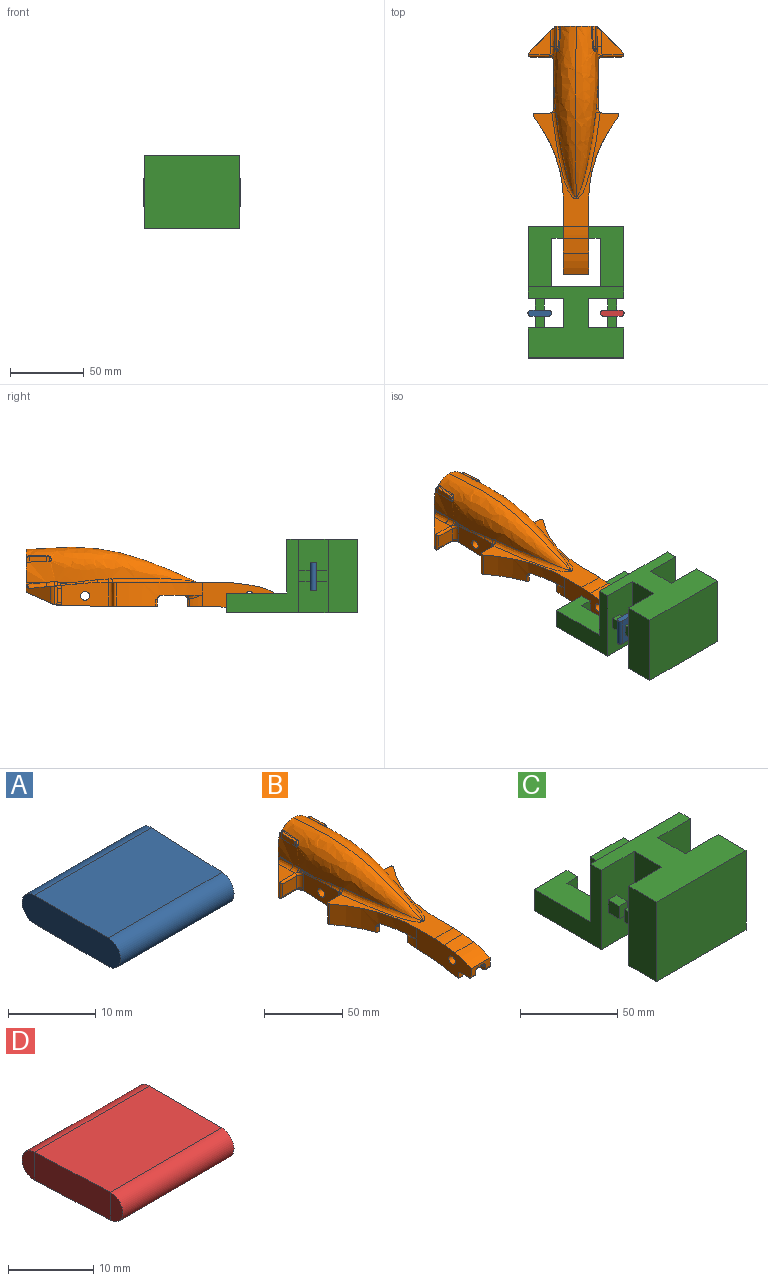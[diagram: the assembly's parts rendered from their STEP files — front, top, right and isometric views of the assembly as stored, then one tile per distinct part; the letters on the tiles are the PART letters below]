
ASSEMBLY  parts=4 mates=3
PART A: 8 faces, bbox 19.1x16x4 mm
  f0: cylinder r=2mm len=18.48mm, axis (-1,0,0), area 115.8mm2, adj f1,f3,f4,f5
  f1: plane 18.99x12mm, normal (0,0,1), area 224.7mm2, adj f0,f2,f4,f6
  f2: cylinder r=2mm len=19.09mm, axis (-1,0,0), area 119.7mm2, adj f1,f3,f4,f7
  f3: plane 18.99x12mm, normal (0,0,-1), area 224.7mm2, adj f0,f2,f4,f6
  f4: plane 16x4mm, normal (-1,0,0), area 60.6mm2, adj f0,f1,f2,f3
  f5: plane 4x2mm, normal (1,-0.04,0), area 6.3mm2, adj f0,f6
  f6: extruded ~12x4mm, area 48mm2, adj f1,f3,f5,f7
  f7: plane 4x2mm, normal (1,-0.05,0), area 6.3mm2, adj f2,f6
PART B: 206 faces, bbox 65.7x176.7x49.3 mm
  f0: extruded ~13.86x1.47mm, area 8mm2, adj f153,f156,f180,f181
  f1: extruded ~13.86x1.47mm, area 8mm2, adj f153,f154,f200,f201
  f2: plane 4.04x2.22mm, normal (-1,0.05,0), area 7.2mm2, adj f154,f158,f159,f167,f179
  f3: plane 3.74x2.02mm, normal (-1,0.04,0), area 6.6mm2, adj f4,f154,f158,f166,f174
  f4: plane 1.69x0.12mm, normal (0,-1,0), area 0.1mm2, adj f3,f154,f174
  f5: plane 12x2.55mm, normal (0,0,1), area 21.9mm2, adj f158,f166,f167,f176
  f6: plane 3.74x2.02mm, normal (1,0.04,0), area 6.6mm2, adj f156,f160,f161,f165,f168
  f7: plane 4.04x2.22mm, normal (1,0.05,0), area 7.2mm2, adj f8,f156,f160,f164,f173
  f8: plane 0.69x0.38mm, normal (0,1,0), area 0.1mm2, adj f7,f164,f173
  f9: plane 12x2.55mm, normal (0,0,1), area 21.9mm2, adj f160,f164,f165,f170
  f10: cylinder r=1.5mm len=7.39mm, axis (-1,0,0), area 10mm2, adj f93,f94,f141,f153
  f11: plane 77.19x58.27mm, normal (0,0,1), area 850.3mm2, adj f37,f38,f43,f45,f46,f47,f51,f52
  f12: cylinder r=1.5mm len=7.39mm, axis (-1,0,0), area 10mm2, adj f27,f84,f129,f153
  f13: plane 16.53x15.09mm, normal (0,0.09,1), area 127mm2, adj f94,f95,f96,f97,f144,f181,f182
  f14: cylinder r=3mm len=17mm, axis (-1,0,0), area 320.4mm2, adj f37,f38
  f15: plane 12.39x5.01mm, normal (0,-0.38,-0.93), area 40.5mm2, adj f16,f69,f99,f100,f101,f109,f110,f111
  f16: cylinder r=3mm len=9.64mm, axis (0,0.93,-0.38), area 38.5mm2, adj f15,f35,f39,f99,f150,f151
  f17: plane 32.43x16.02mm, normal (-1,0,0), area 455.3mm2, adj f31,f44,f64,f76,f82,f145,f146,f147
  f18: plane 17.44x4.22mm, normal (-1,0,0), area 15.6mm2, adj f92,f93,f98,f141
  f19: plane 17.44x4.22mm, normal (1,0,0), area 15.6mm2, adj f27,f28,f82,f129
  f20: plane 8.07x3.26mm, normal (-1,0,0), area 12.7mm2, adj f35,f61,f66,f109
  f21: plane 46.27x9mm, normal (1,0,0), area 142.9mm2, adj f41,f59,f67,f77,f78,f101,f102,f103
  f22: plane 38.6x16.7mm, normal (0,0.24,-0.97), area 601mm2, adj f71,f129,f130,f140,f141,f153
  f23: plane 28.21x4.5mm, normal (1,0,0), area 94.2mm2, adj f31,f50,f76,f123,f124,f125
  f24: cylinder r=30mm len=4.5mm, axis (0,0,-1), area 0.2mm2, adj f32,f54,f75,f133
  f25: plane 12.69x9.72mm, normal (0,-1,0), area 123.3mm2, adj f28,f30,f83,f146
  f26: plane 16.53x15.09mm, normal (0,0.09,1), area 127mm2, adj f30,f84,f85,f87,f147,f199,f200
  f27: plane 22.85x18.63mm, normal (0,0.41,-0.91), area 265.4mm2, adj f12,f19,f28,f84,f85,f129
  f28: cylinder r=1.5mm len=21.69mm, axis (-1,0,0), area 45.4mm2, adj f19,f25,f27,f29,f82,f83,f85,f86
  f29: plane 12.72x0.14mm, normal (-1,0,0), area 1.8mm2, adj f28,f30,f83,f86
  f30: cylinder r=1.5mm len=14.19mm, axis (1,0,0), area 34.1mm2, adj f25,f26,f29,f83,f86,f147
  f31: cylinder r=41.69mm len=4.5mm, axis (1,0,0), area 6.5mm2, adj f17,f23,f76,f82,f126
  f32: plane 28.21x4.5mm, normal (-1,0,0), area 94.2mm2, adj f24,f75,f81,f134,f135,f136
  f33: plane 51.59x25.23mm, normal (0,0,-1), area 736.5mm2, adj f45,f51,f73,f74,f105,f106,f116,f117
  f34: plane 46.27x9mm, normal (-1,0,0), area 142.9mm2, adj f40,f56,f65,f79,f80,f112,f113,f114
  f35: plane 17.01x6.48mm, normal (0,-1,0), area 69.2mm2, adj f16,f20,f37,f38,f39,f60,f61,f62
  f36: plane 32.44x16.02mm, normal (1,0,0), area 455.3mm2, adj f44,f63,f75,f81,f98,f142,f143,f144
  f37: plane 49.36x20.5mm, normal (-1,0,0), area 732.8mm2, adj f11,f14,f35,f41,f42,f43,f45,f58
  f38: plane 49.36x20.5mm, normal (1,0,0), area 732.8mm2, adj f11,f14,f35,f40,f42,f43,f51,f57
  f39: plane 8.07x3.26mm, normal (1,0,0), area 12.7mm2, adj f16,f35,f62,f68
  f40: plane 4x4mm, normal (0,-1,0), area 16mm2, adj f34,f38,f65,f79
  f41: plane 4x4mm, normal (0,-1,0), area 16mm2, adj f21,f37,f67,f78
  f42: plane 17x9.65mm, normal (0,-0.14,0.99), area 165.7mm2, adj f37,f38,f43,f60
  f43: cylinder r=60mm len=17mm, axis (1,0,0), area 144.7mm2, adj f11,f37,f38,f42
  f44: cylinder r=3mm len=30mm, axis (-1,0,0), area 565.5mm2, adj f17,f36
  f45: cylinder r=92.82mm len=57.94mm, axis (0,0,1), area 767.9mm2, adj f11,f33,f37,f47,f49,f76,f107,f108
  f46: plane 16x9.64mm, normal (0,1,0), area 154.2mm2, adj f11,f47,f64,f76
  f47: cylinder r=1.5mm len=16mm, axis (0,0,1), area 53.9mm2, adj f11,f45,f46,f76
  f48: cylinder r=136.18mm len=12.06mm, axis (0,0,-1), area 54.3mm2, adj f49,f50,f76,f121
  f49: cylinder r=1.5mm len=4.5mm, axis (0,0,1), area 18.3mm2, adj f45,f48,f76,f120
  f50: cylinder r=30mm len=4.5mm, axis (0,0,-1), area 0.2mm2, adj f23,f48,f76,f122
  f51: cylinder r=92.82mm len=57.94mm, axis (0,0,1), area 767.9mm2, adj f11,f33,f38,f53,f55,f75,f118,f119
  f52: plane 16x9.64mm, normal (0,1,0), area 154.2mm2, adj f11,f53,f63,f75
  f53: cylinder r=1.5mm len=16mm, axis (0,0,1), area 53.9mm2, adj f11,f51,f52,f75
  f54: cylinder r=136.18mm len=12.06mm, axis (0,0,-1), area 54.3mm2, adj f24,f55,f75,f132
  f55: cylinder r=1.5mm len=4.5mm, axis (0,0,1), area 18.3mm2, adj f51,f54,f75,f131
  f56: cylinder r=1.5mm len=4.84mm, axis (0,0,-1), area 19.8mm2, adj f34,f57,f80,f117,f118
  f57: cylinder r=37.75mm len=8.81mm, axis (0,0,-1), area 54.8mm2, adj f38,f56,f80,f119
  f58: cylinder r=37.75mm len=8.81mm, axis (0,0,-1), area 54.8mm2, adj f37,f59,f77,f108
  f59: cylinder r=1.5mm len=4.84mm, axis (0,0,-1), area 19.8mm2, adj f21,f58,f77,f106,f107
  f60: cylinder r=42.58mm len=17mm, axis (-1,0,0), area 268.4mm2, adj f35,f37,f38,f42
  f61: cylinder r=1.5mm len=4mm, axis (-1,0,0), area 9.4mm2, adj f20,f35,f38,f66
  f62: cylinder r=1.5mm len=4mm, axis (-1,0,0), area 9.4mm2, adj f35,f37,f39,f68
  f63: cylinder r=3mm len=16mm, axis (0,0,1), area 75.4mm2, adj f11,f36,f52,f75,f189
  f64: cylinder r=3mm len=16mm, axis (0,0,1), area 75.4mm2, adj f11,f17,f46,f76,f192
  f65: cylinder r=1.5mm len=4mm, axis (-1,0,0), area 9.4mm2, adj f34,f38,f40,f66,f111
  f66: plane 8.57x4.03mm, normal (0,0,-1), area 34.2mm2, adj f20,f38,f61,f65,f110
  f67: cylinder r=1.5mm len=4mm, axis (-1,0,0), area 9.4mm2, adj f21,f37,f41,f68,f100
  f68: plane 8.57x4.03mm, normal (0,0,-1), area 34.2mm2, adj f37,f39,f62,f67,f99
  f69: cylinder r=6mm len=3.81mm, axis (1,0,0), area 11.6mm2, adj f15,f70,f102,f113
  f70: plane 17.07x4.58mm, normal (0,0.26,-0.97), area 53mm2, adj f69,f74,f103,f114
  f71: cylinder r=6mm len=16.69mm, axis (1,0,0), area 55.6mm2, adj f22,f72,f128,f139
  f72: plane 16.03x10.19mm, normal (0,-0.32,-0.95), area 163.1mm2, adj f71,f73,f125,f126,f127,f136,f137,f138
  f73: cylinder r=50mm len=16.18mm, axis (-1,0,0), area 247.2mm2, adj f33,f72,f124,f135
  f74: cylinder r=50mm len=12.97mm, axis (1,0,0), area 39.3mm2, adj f33,f70,f104,f115
  f75: plane 40.66x18.64mm, normal (0,0,-1), area 358mm2, adj f24,f32,f36,f51,f52,f53,f54,f55
  f76: plane 40.66x18.64mm, normal (0,0,-1), area 358mm2, adj f17,f23,f31,f45,f46,f47,f48,f49
  f77: plane 9.96x4mm, normal (0,0,-1), area 34.7mm2, adj f21,f58,f59,f78
  f78: cylinder r=161.13mm len=37.81mm, axis (-1,0,0), area 152.7mm2, adj f21,f37,f41,f77
  f79: cylinder r=161.13mm len=37.81mm, axis (-1,0,0), area 152.7mm2, adj f34,f38,f40,f80
  f80: plane 9.96x4mm, normal (0,0,-1), area 34.7mm2, adj f34,f56,f57,f79
  f81: cylinder r=41.69mm len=4.5mm, axis (1,0,0), area 6.5mm2, adj f32,f36,f75,f98,f137
  f82: plane 28.76x8.77mm, normal (0,0.03,-1), area 127.9mm2, adj f17,f19,f28,f31,f127,f128,f130,f145
  f83: cylinder r=1.5mm len=12.72mm, axis (0,0,1), area 26.4mm2, adj f25,f28,f29,f30
  f84: plane 17.79x17.79mm, normal (-0.71,0.71,0), area 163.3mm2, adj f12,f26,f27,f85,f153,f200,f201
  f85: cylinder r=6mm len=12.61mm, axis (0,0,1), area 33.8mm2, adj f26,f27,f28,f84,f87
  f86: plane 12.7x0.01mm, normal (0,1,0), area 0.1mm2, adj f28,f29,f30,f87
  f87: cylinder r=1.5mm len=12.7mm, axis (0,0,1), area 4.2mm2, adj f26,f28,f85,f86
  f88: plane 12.7x0.01mm, normal (0,1,0), area 0.1mm2, adj f89,f92,f96,f97
  f89: plane 12.72x0.14mm, normal (1,0,0), area 1.8mm2, adj f88,f90,f92,f97
  f90: cylinder r=1.5mm len=12.72mm, axis (0,0,1), area 26.4mm2, adj f89,f91,f92,f97
  f91: plane 12.69x9.72mm, normal (0,-1,0), area 123.3mm2, adj f90,f92,f97,f143
  f92: cylinder r=1.5mm len=21.69mm, axis (1,0,0), area 45.4mm2, adj f18,f88,f89,f90,f91,f93,f95,f96
  f93: plane 22.85x18.63mm, normal (0,0.41,-0.91), area 265.4mm2, adj f10,f18,f92,f94,f95,f141
  f94: plane 17.78x17.78mm, normal (0.71,0.71,0), area 163.3mm2, adj f10,f13,f93,f95,f153,f180,f181
  f95: cylinder r=6mm len=12.61mm, axis (0,0,1), area 33.8mm2, adj f13,f92,f93,f94,f96
  f96: cylinder r=1.5mm len=12.7mm, axis (0,0,1), area 4.2mm2, adj f13,f88,f92,f95
  f97: cylinder r=1.5mm len=14.19mm, axis (-1,0,0), area 34.1mm2, adj f13,f88,f89,f90,f91,f144
  f98: plane 28.76x8.77mm, normal (0,0.03,-1), area 127.9mm2, adj f18,f36,f81,f92,f138,f139,f140,f142
  f99: bspline ~3.57x3.08mm, area 8.4mm2, adj f15,f16,f68,f100
  f100: bspline ~3.59x3.03mm, area 7.3mm2, adj f15,f67,f99,f101
  f101: cylinder r=3mm len=3.72mm, axis (0,0.93,-0.38), area 11.8mm2, adj f15,f21,f100,f102
  f102: torus R=9mm, axis (-1,0,0), area 21.6mm2, adj f21,f69,f101,f103
  f103: cylinder r=3mm len=17.85mm, axis (0,0.97,0.26), area 83.3mm2, adj f21,f70,f102,f104
  f104: torus R=47mm, axis (-1,0,0), area 60.5mm2, adj f21,f74,f103,f105
  f105: cylinder r=3mm len=8.98mm, axis (0,-1,0), area 42.3mm2, adj f21,f33,f104,f106
  f106: torus R=4.5mm, axis (0,0,1), area 28.9mm2, adj f33,f59,f105,f107
  f107: bspline ~3x2.79mm, area 3.8mm2, adj f45,f59,f106,f108
  f108: bspline ~10.19x2.76mm, area 10.1mm2, adj f45,f58,f107
  f109: cylinder r=3mm len=9.64mm, axis (0,0.93,-0.38), area 38.5mm2, adj f15,f20,f35,f110,f148,f149
  f110: bspline ~5.08x3.46mm, area 8.4mm2, adj f15,f66,f109,f111
  f111: bspline ~3.59x3.03mm, area 7.3mm2, adj f15,f65,f110,f112
  f112: cylinder r=3mm len=3.72mm, axis (0,0.93,-0.38), area 11.8mm2, adj f15,f34,f111,f113
  f113: torus R=9mm, axis (1,0,0), area 21.6mm2, adj f34,f69,f112,f114
  f114: cylinder r=3mm len=17.85mm, axis (0,0.97,0.26), area 83.3mm2, adj f34,f70,f113,f115
  f115: torus R=47mm, axis (1,0,0), area 60.5mm2, adj f34,f74,f114,f116
  f116: cylinder r=3mm len=8.98mm, axis (0,1,0), area 42.3mm2, adj f33,f34,f115,f117
  f117: torus R=4.5mm, axis (0,0,1), area 28.9mm2, adj f33,f56,f116,f118
  f118: bspline ~3x2.79mm, area 3.8mm2, adj f51,f56,f117,f119
  f119: bspline ~10.19x2.76mm, area 10.1mm2, adj f51,f57,f118
  f120: torus R=4.5mm, axis (0,0,1), area 24.2mm2, adj f33,f45,f49,f121
  f121: torus R=139.18mm, axis (0,0,1), area 57.4mm2, adj f33,f48,f120,f122
  f122: torus R=33mm, axis (0,0,1), area 0.2mm2, adj f33,f50,f121,f123
  f123: cylinder r=3mm len=7.28mm, axis (0,-1,0), area 34.3mm2, adj f23,f33,f122,f124
  f124: torus R=47mm, axis (-1,0,0), area 76mm2, adj f23,f73,f123,f125
  f125: cylinder r=3mm len=6.7mm, axis (0,0.95,-0.32), area 28.5mm2, adj f23,f72,f124,f126
  f126: bspline ~3x2.84mm, area 1.9mm2, adj f31,f72,f125,f127
  f127: bspline ~6.39x3.02mm, area 15.1mm2, adj f72,f82,f126,f128
  f128: bspline ~5.87x2.57mm, area 9.8mm2, adj f71,f82,f127,f130
  f129: cylinder r=3mm len=29.22mm, axis (0,-0.97,-0.24), area 121.9mm2, adj f12,f19,f22,f27,f130,f204
  f130: bspline ~10.78x3.27mm, area 36.9mm2, adj f22,f82,f128,f129
  f131: torus R=4.5mm, axis (0,0,1), area 24.2mm2, adj f33,f51,f55,f132
  f132: torus R=139.18mm, axis (0,0,1), area 57.4mm2, adj f33,f54,f131,f133
  f133: torus R=33mm, axis (0,0,1), area 0.2mm2, adj f24,f33,f132,f134
  f134: cylinder r=3mm len=7.28mm, axis (0,1,0), area 34.3mm2, adj f32,f33,f133,f135
  f135: torus R=47mm, axis (1,0,0), area 76mm2, adj f32,f73,f134,f136
  f136: cylinder r=3mm len=6.7mm, axis (0,0.95,-0.32), area 28.5mm2, adj f32,f72,f135,f137
  f137: bspline ~3.19x3.04mm, area 2mm2, adj f72,f81,f136,f138
  f138: bspline ~6.42x3.08mm, area 15.1mm2, adj f72,f98,f137,f139
  f139: bspline ~5.01x2.49mm, area 9.8mm2, adj f71,f98,f138,f140
  f140: bspline ~12.73x3.61mm, area 36.9mm2, adj f22,f98,f139,f141
  f141: cylinder r=3mm len=29.22mm, axis (0,-0.97,-0.24), area 121.9mm2, adj f10,f18,f22,f93,f140,f203
  f142: torus R=4.5mm, axis (-1,0,0), area 10.6mm2, adj f36,f92,f98,f143
  f143: cylinder r=3mm len=9.72mm, axis (0,0,1), area 45.8mm2, adj f36,f91,f142,f144
  f144: torus R=4.5mm, axis (-1,0,0), area 9.3mm2, adj f13,f36,f97,f143,f183,f184
  f145: torus R=4.5mm, axis (1,0,0), area 10.6mm2, adj f17,f28,f82,f146
  f146: cylinder r=3mm len=9.72mm, axis (0,0,1), area 45.8mm2, adj f17,f25,f145,f147
  f147: torus R=4.5mm, axis (1,0,0), area 9.3mm2, adj f17,f26,f30,f146,f197,f198
  f148: extruded ~4.21x2.6mm, area 9mm2, adj f15,f109,f149,f150,f152
  f149: extruded ~0.17x0.06mm, area 0mm2, adj f109,f148,f152
  f150: extruded ~4.21x2.6mm, area 9.1mm2, adj f15,f16,f148,f151,f152
  f151: extruded ~0.17x0.06mm, area 0mm2, adj f16,f150,f152
  f152: plane 8.57x1.99mm, normal (0,-1,0), area 7.2mm2, adj f35,f148,f149,f150,f151
  f153: plane 28.14x28.14mm, normal (0,1,0), area 416.3mm2, adj f0,f1,f10,f12,f22,f84,f94,f154
  f154: bspline ~127x31.96mm, area 2576.2mm2, adj f1,f2,f3,f4,f153,f155,f156,f158
  f155: extruded ~11.89x0.9mm, area 5.3mm2, adj f154,f196,f197
  f156: bspline ~127x31.96mm, area 2576.2mm2, adj f0,f6,f7,f153,f154,f157,f160,f161
  f157: extruded ~11.89x0.9mm, area 5.3mm2, adj f156,f184,f185
  f158: extruded ~12x3.96mm, area 46.2mm2, adj f2,f3,f5,f154
  f159: plane 0.69x0.38mm, normal (0,1,0), area 0.1mm2, adj f2,f167,f179
  f160: extruded ~12x3.96mm, area 46.2mm2, adj f6,f7,f9,f156
  f161: plane 1.69x0.12mm, normal (0,-1,0), area 0.1mm2, adj f6,f156,f168
  f162: cylinder r=9.5mm len=52mm, axis (0,1,0), area 3103.9mm2, adj f153,f163
  f163: plane 19x19mm, normal (0,1,0), area 283.5mm2, adj f162
  f164: cylinder r=2mm len=2.05mm, axis (1,0,0), area 4.3mm2, adj f7,f8,f9,f171,f172
  f165: cylinder r=2mm len=1.94mm, axis (1,0,0), area 2.2mm2, adj f6,f9,f169
  f166: cylinder r=2mm len=1.94mm, axis (-1,0,0), area 2.2mm2, adj f3,f5,f175
  f167: cylinder r=2mm len=2.05mm, axis (-1,0,0), area 4.3mm2, adj f2,f5,f159,f177,f178
  f168: bspline ~2.16x1.32mm, area 1.8mm2, adj f6,f156,f161,f169
  f169: bspline ~3.49x2.7mm, area 4.1mm2, adj f156,f165,f168,f170
  f170: bspline ~18.69x2.11mm, area 10.2mm2, adj f9,f156,f169,f171
  f171: bspline ~3.11x1.85mm, area 2mm2, adj f156,f164,f170,f172
  f172: bspline ~2.59x2.33mm, area 1.3mm2, adj f153,f164,f171,f173
  f173: bspline ~4.3x2.69mm, area 0.8mm2, adj f7,f8,f153,f172
  f174: bspline ~2.16x1.32mm, area 1.8mm2, adj f3,f4,f154,f175
  f175: bspline ~3.49x2.7mm, area 4.1mm2, adj f154,f166,f174,f176
  f176: bspline ~16.2x1.9mm, area 10.2mm2, adj f5,f154,f175,f177
  f177: bspline ~3.11x1.85mm, area 2mm2, adj f154,f167,f176,f178
  f178: bspline ~2.59x2.33mm, area 1.3mm2, adj f153,f167,f177,f179
  f179: bspline ~3.82x2.17mm, area 0.8mm2, adj f2,f153,f159,f178
  f180: bspline ~3.25x3.09mm, area 1.4mm2, adj f0,f94,f181
  f181: bspline ~31.24x5.91mm, area 58.4mm2, adj f0,f13,f94,f180,f182
  f182: bspline ~19.48x4.8mm, area 26.3mm2, adj f13,f156,f181,f183
  f183: bspline ~3.01x3mm, area 6.5mm2, adj f144,f156,f182,f184
  f184: bspline ~2.9x2.43mm, area 4.8mm2, adj f144,f157,f183,f185
  f185: bspline ~10.39x2.18mm, area 12.8mm2, adj f36,f157,f184,f186
  f186: bspline ~5.5x1.91mm, area 7.2mm2, adj f36,f156,f185,f187
  f187: bspline ~26.16x4.72mm, area 17mm2, adj f36,f156,f186,f188
  f188: bspline ~11.15x2.64mm, area 18.7mm2, adj f36,f156,f187,f189
  f189: bspline ~3.11x3.11mm, area 8.8mm2, adj f63,f156,f188,f190
  f190: bspline ~68.92x18.36mm, area 252.7mm2, adj f11,f156,f189,f191
  f191: bspline ~68.92x17.55mm, area 252.7mm2, adj f11,f154,f190,f192
  f192: bspline ~3.11x3.11mm, area 8.8mm2, adj f64,f154,f191,f193
  f193: bspline ~11.15x2.64mm, area 18.7mm2, adj f17,f154,f192,f194
  f194: bspline ~19.22x3.73mm, area 17mm2, adj f17,f154,f193,f195
  f195: bspline ~5.5x1.91mm, area 7.2mm2, adj f17,f154,f194,f196
  f196: bspline ~10.39x2.18mm, area 12.8mm2, adj f17,f155,f195,f197
  f197: bspline ~3.46x2.58mm, area 4.8mm2, adj f147,f155,f196,f198
  f198: bspline ~3.01x3mm, area 6.5mm2, adj f147,f154,f197,f199
  f199: bspline ~5.77x3.51mm, area 26.3mm2, adj f26,f154,f198,f200
  f200: bspline ~31.24x5.91mm, area 58.4mm2, adj f1,f26,f84,f199,f201
  f201: bspline ~3.25x3.09mm, area 1.4mm2, adj f1,f84,f200
  f202: plane 1.5x1.5mm, normal (-1,0,0), area 1.8mm2, adj f203
  f203: cylinder r=0.75mm len=5.34mm, axis (1,0,0), area 23mm2, adj f141,f202
  f204: cylinder r=0.75mm len=5.34mm, axis (1,0,0), area 23mm2, adj f129,f205
  f205: plane 1.5x1.5mm, normal (1,0,0), area 1.8mm2, adj f204
PART C: 46 faces, bbox 65x89.3x50 mm
  f0: plane 50x20.26mm, normal (1,0,0), area 1013.2mm2, adj f2,f7,f8,f25
  f1: plane 50x20.26mm, normal (-1,0,0), area 1013.2mm2, adj f2,f7,f8,f20
  f2: plane 65x48.26mm, normal (0,0,1), area 2177.2mm2, adj f0,f1,f3,f5,f6,f8,f20,f21
  f3: plane 65x50mm, normal (0,1,0), area 2818.9mm2, adj f2,f4,f5,f6,f7,f10,f14,f16
  f4: plane 41x13.47mm, normal (-1,0,0), area 488.4mm2, adj f3,f7,f9,f10,f12,f13
  f5: plane 50x49mm, normal (1,0,0), area 952.4mm2, adj f2,f3,f7,f9,f10,f23
  f6: plane 50x49mm, normal (-1,0,0), area 952.4mm2, adj f2,f3,f7,f15,f16,f22
  f7: plane 89.26x65mm, normal (0,0,-1), area 3489.2mm2, adj f0,f1,f3,f4,f5,f6,f8,f9
  f8: plane 65x50mm, normal (0,-1,0), area 3250mm2, adj f0,f1,f2,f7
  f9: plane 24x13.47mm, normal (0,1,0), area 279.6mm2, adj f4,f5,f7,f10,f11,f12
  f10: plane 41x24mm, normal (0,0,1), area 720mm2, adj f3,f4,f5,f9,f11,f13
  f11: plane 8x8mm, normal (-1,0,0), area 64mm2, adj f9,f10,f12,f13
  f12: plane 8x8mm, normal (0,0,-1), area 64mm2, adj f4,f9,f11,f13
  f13: plane 8x8mm, normal (0,-1,0), area 64mm2, adj f4,f10,f11,f12
  f14: plane 41x13.47mm, normal (1,0,0), area 488.4mm2, adj f3,f7,f15,f16,f18,f19
  f15: plane 24x13.47mm, normal (0,1,0), area 279.6mm2, adj f6,f7,f14,f16,f17,f18
  f16: plane 41x24mm, normal (0,0,1), area 720mm2, adj f3,f6,f14,f15,f17,f19
  f17: plane 8x8mm, normal (1,0,0), area 64mm2, adj f15,f16,f18,f19
  f18: plane 8x8mm, normal (0,0,-1), area 64mm2, adj f14,f15,f17,f19
  f19: plane 8x8mm, normal (0,-1,0), area 64mm2, adj f14,f16,f17,f18
  f20: plane 50x24mm, normal (0,1,0), area 1152mm2, adj f1,f2,f7,f21,f37,f38,f39,f40
  f21: plane 50x20mm, normal (-1,0,0), area 1000mm2, adj f2,f7,f20,f22
  f22: plane 50x24mm, normal (0,-1,0), area 1152mm2, adj f2,f6,f7,f21,f27,f28,f29,f30
  f23: plane 50x24mm, normal (0,-1,0), area 1152mm2, adj f2,f5,f7,f24,f32,f33,f34,f35
  f24: plane 50x20mm, normal (1,0,0), area 1000mm2, adj f2,f7,f23,f25
  f25: plane 50x24mm, normal (0,1,0), area 1152mm2, adj f0,f2,f7,f24,f42,f43,f44,f45
  f26: plane 8x6mm, normal (0,-1,0), area 48mm2, adj f27,f28,f29,f30
  f27: plane 8x8mm, normal (1,0,0), area 64mm2, adj f22,f26,f28,f30
  f28: plane 8x6mm, normal (0,0,1), area 48mm2, adj f22,f26,f27,f29
  f29: plane 8x8mm, normal (-1,0,0), area 64mm2, adj f22,f26,f28,f30
  f30: plane 8x6mm, normal (0,0,-1), area 48mm2, adj f22,f26,f27,f29
  f31: plane 8x6mm, normal (0,-1,0), area 48mm2, adj f32,f33,f34,f35
  f32: plane 8x6mm, normal (0,0,1), area 48mm2, adj f23,f31,f33,f35
  f33: plane 8x8mm, normal (-1,0,0), area 64mm2, adj f23,f31,f32,f34
  f34: plane 8x6mm, normal (0,0,-1), area 48mm2, adj f23,f31,f33,f35
  f35: plane 8x8mm, normal (1,0,0), area 64mm2, adj f23,f31,f32,f34
  f36: plane 8x6mm, normal (0,1,0), area 48mm2, adj f37,f38,f39,f40
  f37: plane 8x6mm, normal (0,0,1), area 48mm2, adj f20,f36,f38,f39
  f38: plane 8x8mm, normal (1,0,0), area 64mm2, adj f20,f36,f37,f40
  f39: plane 8x8mm, normal (-1,0,0), area 64mm2, adj f20,f36,f37,f40
  f40: plane 8x6mm, normal (0,0,-1), area 48mm2, adj f20,f36,f38,f39
  f41: plane 8x6mm, normal (0,1,0), area 48mm2, adj f42,f43,f44,f45
  f42: plane 8x8mm, normal (-1,0,0), area 64mm2, adj f25,f41,f43,f45
  f43: plane 8x6mm, normal (0,0,1), area 48mm2, adj f25,f41,f42,f44
  f44: plane 8x8mm, normal (1,0,0), area 64mm2, adj f25,f41,f43,f45
  f45: plane 8x6mm, normal (0,0,-1), area 48mm2, adj f25,f41,f42,f44
PART D: 8 faces, bbox 19.1x16x4 mm
  f0: plane 16x4mm, normal (1,0,0), area 60.6mm2, adj f1,f2,f3,f4
  f1: plane 18.99x12mm, normal (0,0,-1), area 224.7mm2, adj f0,f3,f4,f5
  f2: plane 18.99x12mm, normal (0,0,1), area 224.7mm2, adj f0,f3,f4,f5
  f3: cylinder r=2mm len=18.48mm, axis (1,0,0), area 115.8mm2, adj f0,f1,f2,f6
  f4: cylinder r=2mm len=19.09mm, axis (1,0,0), area 119.7mm2, adj f0,f1,f2,f7
  f5: extruded ~12x4mm, area 48mm2, adj f1,f2,f6,f7
  f6: plane 4x2mm, normal (-1,-0.04,0), area 6.3mm2, adj f3,f5
  f7: plane 4x2mm, normal (-1,-0.05,0), area 6.3mm2, adj f4,f5
PLACE A rot(axis=(-0.58,0.58,0.58),120deg) t=(-6.79,-98.4,-14.39)mm
PLACE B t=(25.96,103.76,12.25)mm
PLACE C t=(25.96,-72.97,8.25)mm
PLACE D rot(axis=(-0.58,-0.58,-0.58),120deg) t=(58.72,-98.4,-14.39)mm
MATE fastened C.f11 <-> B.f38  axis (-1,0,0) through (34.46,-39.97,-3.28)mm
MATE fastened A.f1 <-> C.f26  axis (0,1,0) through (1.36,-88.97,8.25)mm
MATE fastened D.f2 <-> C.f31  axis (0,1,0) through (50.57,-88.97,8.25)mm
